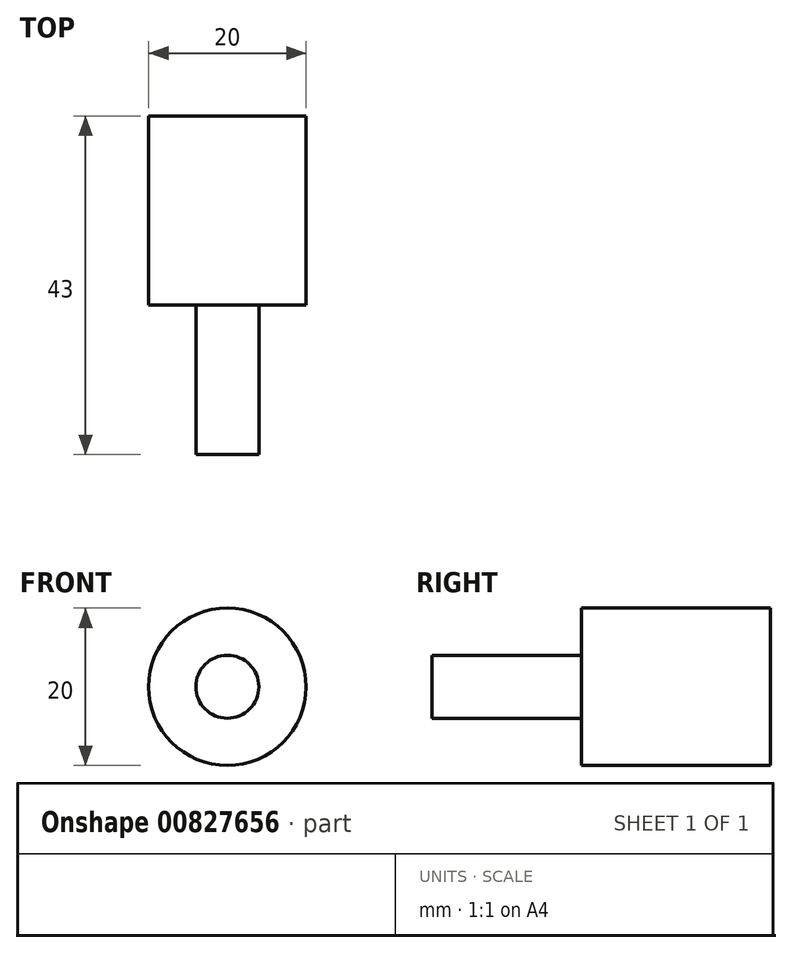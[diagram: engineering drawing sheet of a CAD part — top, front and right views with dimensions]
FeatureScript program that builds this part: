
annotation { "Feature Type Name" : "Feature", "Feature Type Description" : "" }
export const myFeature = defineFeature(function(context is Context, id is Id, definition is map)
    precondition{}
    {
        {
            var Q0;
            Q0=qCreatedBy(makeId("Front.planeOp"),FACE);
            var sketch = newSketch(context, id + "F0", { "sketchPlane" : qUnion([Q0])});
            skCircle(sketch, "E0", {"center": v(0, 0) * mm, "radius": 10 * mm});
            skSolve(sketch);
        }
        {
            var Q0;
            Q0=makeQuery(id+"F0.imprint","IMPRINT",FACE,{"disambiguationData":[TD([[makeQuery(id+"F0.imprint","IMPRINT",EDGE,{"derivedFrom":sQuery(id+"F0.wireOp",EDGE,"E0")}),1.0]])]});
            extrude(context, id + "F1", {"entities" : qUnion([Q0]), "depth" : (48 / 2) * mm, "offsetDistance" : 25 * mm});
        }
        {
            var Q0;
            Q0=makeQuery(id+"F1.opExtrude","CAP_FACE",FACE,{"disambiguationData":[OSD([sQuery(id+"F0.wireOp",EDGE,"E0")])],"isStart":false});
            var sketch = newSketch(context, id + "F2", { "sketchPlane" : qUnion([Q0])});
            skCircle(sketch, "E1", {"center": v(0, 0) * mm, "radius": 4 * mm});
            skSolve(sketch);
        }
        {
            var Q0;
            Q0=makeQuery(id+"F2.imprint","IMPRINT",FACE,{"disambiguationData":[TD([[makeQuery(id+"F2.imprint","IMPRINT",EDGE,{"derivedFrom":sQuery(id+"F2.wireOp",EDGE,"E1")}),1.0]])]});
            extrude(context, id + "F3", {"entities" : qUnion([Q0]), "operationType" : NewBodyOperationType.ADD, "depth" : 19 * mm, "offsetDistance" : 25 * mm});
        }
    });
